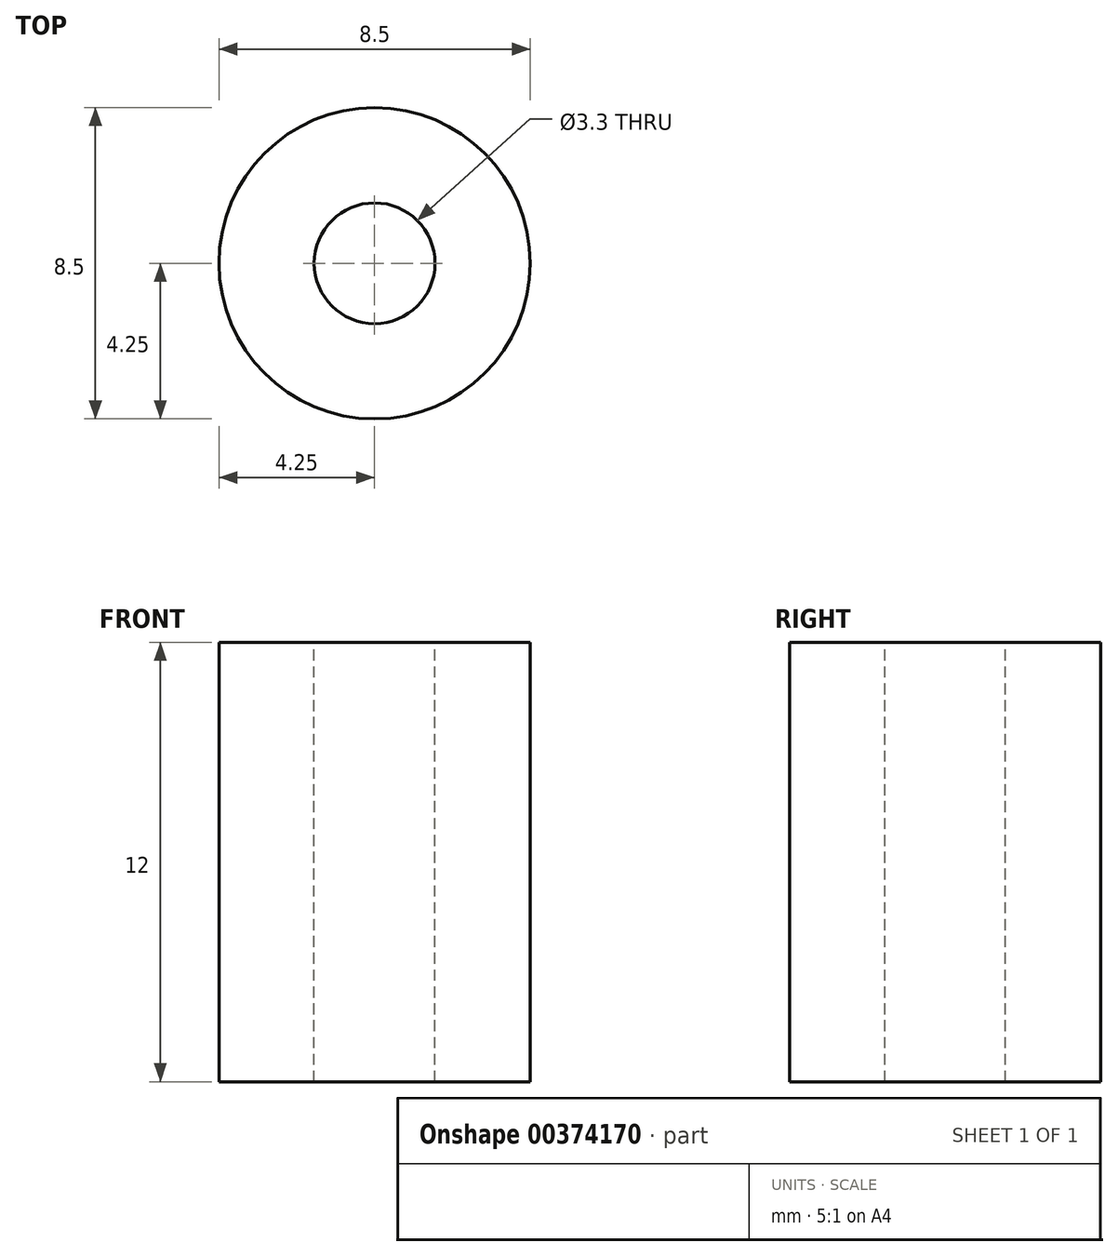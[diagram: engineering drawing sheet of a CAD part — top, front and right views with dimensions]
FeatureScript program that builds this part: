
annotation { "Feature Type Name" : "Feature", "Feature Type Description" : "" }
export const myFeature = defineFeature(function(context is Context, id is Id, definition is map)
    precondition{}
    {
        {
            var Q0;
            Q0=qCreatedBy(makeId("Top.planeOp"),FACE);
            var sketch = newSketch(context, id + "F0", { "sketchPlane" : qUnion([Q0])});
            skCircle(sketch, "E0", {"center": v(0, 0) * mm, "radius": 4.25 * mm});
            skSolve(sketch);
        }
        {
            var Q0;
            Q0=makeQuery(id+"F0.imprint","IMPRINT",FACE,{"disambiguationData":[TD([[makeQuery(id+"F0.imprint","IMPRINT",EDGE,{"derivedFrom":sQuery(id+"F0.wireOp",EDGE,"E0")}),1.0]])]});
            extrude(context, id + "F1", {"entities" : qUnion([Q0]), "oppositeDirection" : true, "depth" : 12 * mm});
        }
        {
            var Q0;
            Q0=makeQuery(id+"F1.opExtrude","CAP_FACE",FACE,{"disambiguationData":[OSD([sQuery(id+"F0.wireOp",EDGE,"E0")])],"isStart":true});
            var sketch = newSketch(context, id + "F2", { "sketchPlane" : qUnion([Q0])});
            skPoint(sketch, "E1", {"position": v(0, 0) * mm});
            skSolve(sketch);
        }
        {
            var Q0;
            Q0=sQuery(id+"F2.wireOp",VERTEX,"E1");
            var Q1;
            Q1=makeQuery(id+"F1.opExtrude","SWEPT_BODY",BODY,{"disambiguationData":[OSD([sQuery(id+"F0.wireOp",EDGE,"E0")])]});
            hole(context, id + "F3", {"style" : HoleStyle.SIMPLE, "endStyle" : HoleEndStyle.THROUGH, "standardTappedOrClearance" : lookupTablePath({ "standard" : "ISO", "fit" : "Normal", "size" : "M3", "type" : "Clearance" }), "standardBlindInLast" : lookupTablePath({ "fit" : "Standard", "standard" : "ISO", "size" : "M3", "type" : "Clearance" }), "holeDiameter" : 3.3 * mm, "isTappedThrough" : true, "tappedDepth" : 12 * mm, "tapClearance" : 3, "locations" : qUnion([Q0]), "scope" : qUnion([Q1])});
        }
    });
